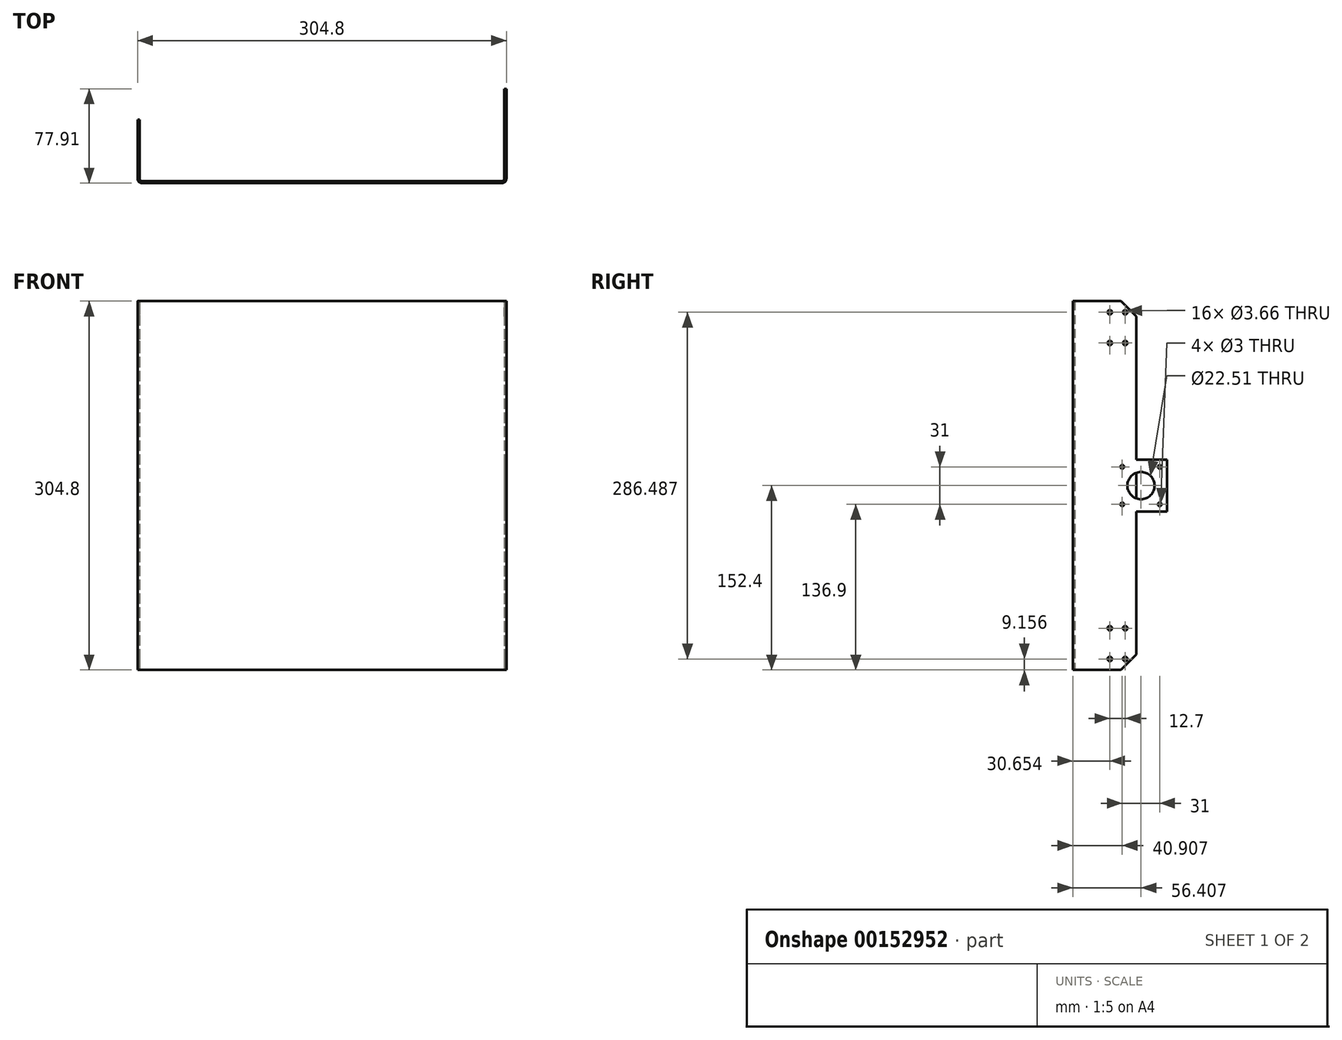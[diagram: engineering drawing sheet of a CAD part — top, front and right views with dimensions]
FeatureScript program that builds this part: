
annotation { "Feature Type Name" : "Feature", "Feature Type Description" : "" }
export const myFeature = defineFeature(function(context is Context, id is Id, definition is map)
    precondition{}
    {
        {
            var Q0;
            Q0=qCreatedBy(makeId("Top.planeOp"),FACE);
            var sketch = newSketch(context, id + "F0", { "sketchPlane" : qUnion([Q0])});
            skLineSegment(sketch, "E0.bottom", {"start": v(0, 0) * mm, "end": v(-301.38, 0) * mm});
            skLineSegment(sketch, "E0.top", {"start": v(1.7, -1.7) * mm, "end": v(-303.1, -1.7) * mm});
            skLineSegment(sketch, "E1.top", {"start": v(-301.38, 50.8) * mm, "end": v(-303.1, 50.8) * mm});
            skLineSegment(sketch, "E1.left", {"start": v(-301.38, 0) * mm, "end": v(-301.38, 50.8) * mm});
            skLineSegment(sketch, "E1.right", {"start": v(-303.1, -1.7) * mm, "end": v(-303.1, 50.8) * mm});
            skLineSegment(sketch, "E2.top", {"start": v(0, 50.8) * mm, "end": v(1.7, 50.8) * mm});
            skLineSegment(sketch, "E2.left", {"start": v(0, 0) * mm, "end": v(0, 50.8) * mm});
            skLineSegment(sketch, "E2.right", {"start": v(1.7, -1.7) * mm, "end": v(1.7, 50.8) * mm});
            skLineSegment(sketch, "E3", {"start": v(-150.7, 0) * mm, "end": v(-150.7, -1.7) * mm, "construction": true});
            skSolve(sketch);
        }
        {
            var Q0;
            Q0=qSketchRegion(id+"F0",true);
            extrude(context, id + "F1", {"entities" : qUnion([Q0]), "depth" : 304.8 * mm});
        }
        {
            var Q0;
            Q0=makeQuery(id+"F1.opExtrude","SWEPT_EDGE",EDGE,{"disambiguationData":[OSD([sQuery(id+"F0.wireOp",EDGE,"E0.top"),sQuery(id+"F0.wireOp",EDGE,"E2.right")])]});
            var Q1;
            Q1=makeQuery(id+"F1.opExtrude","SWEPT_EDGE",EDGE,{"disambiguationData":[OSD([sQuery(id+"F0.wireOp",EDGE,"E0.top"),sQuery(id+"F0.wireOp",EDGE,"E1.right")])]});
            var Q2;
            Q2=makeQuery(id+"FqNnmMD7oaRdpTN_1.opExtrude","CAP_EDGE",EDGE,{"disambiguationData":[OSD([sQuery(id+"FY5sMr6MULj5lJw_1.wireOp",EDGE,"W42EfhJi-fDm4-L9BW-folL-irsYfDskuzBk.top")])],"isStart":false});
            fillet(context, id + "F2", {"entities" : qUnion([Q0, Q1, Q2]), "radius" : 3.7 * mm, "tangentPropagation" : true, "allowEdgeOverflow" : false});
        }
        {
            var Q0;
            Q0=makeQuery(id+"F1.opExtrude","SWEPT_EDGE",EDGE,{"disambiguationData":[OSD([sQuery(id+"F0.wireOp",EDGE,"E0.bottom"),sQuery(id+"F0.wireOp",EDGE,"E2.left")])]});
            var Q1;
            Q1=makeQuery(id+"F1.opExtrude","SWEPT_EDGE",EDGE,{"disambiguationData":[OSD([sQuery(id+"F0.wireOp",EDGE,"E0.bottom"),sQuery(id+"F0.wireOp",EDGE,"E1.left")])]});
            var Q2;
            Q2=makeQuery(id+"FINw0yXB7tfJ6ph_1.opExtrude","CAP_EDGE",EDGE,{"disambiguationData":[OSD([sQuery(id+"FXTh39mUIuS7Wju_1.wireOp",EDGE,"hp9PxWrt-gqSh-sbC0-0nHm-23euh1xvblPI.top")])],"isStart":true});
            fillet(context, id + "F3", {"entities" : qUnion([Q0, Q1, Q2]), "radius" : 1.98 * mm, "tangentPropagation" : true, "allowEdgeOverflow" : false});
        }
        {
            var Q0;
            Q0=makeQuery(id+"F1.opExtrude","SWEPT_FACE",FACE,{"disambiguationData":[OSD([sQuery(id+"F0.wireOp",EDGE,"E2.top")])]});
            var sketch = newSketch(context, id + "F4", { "sketchPlane" : qUnion([Q0])});
            skLineSegment(sketch, "E4.bottom", {"start": v(0, 173.9) * mm, "end": v(-1.7, 173.9) * mm});
            skLineSegment(sketch, "E4.top", {"start": v(0, 130.9) * mm, "end": v(-1.7, 130.9) * mm});
            skLineSegment(sketch, "E4.left", {"start": v(0, 173.9) * mm, "end": v(0, 130.9) * mm});
            skLineSegment(sketch, "E4.right", {"start": v(-1.7, 173.9) * mm, "end": v(-1.7, 130.9) * mm});
            skPoint(sketch, "E5", {"position": v(-1.7, 152.4) * mm});
            skSolve(sketch);
        }
        {
            var Q0;
            Q0 = qSketchRegion(id + "F4", true);
            extrude(context, id + "F5", {"entities" : qUnion([Q0]), "operationType" : NewBodyOperationType.ADD, "depth" : 25.4 * mm});
        }
        {
            var Q0;
            Q0=makeQuery(id+"F5.boolean.opBoolean","MERGE",FACE,{"derivedFrom":[makeQuery(id+"F1.opExtrude","SWEPT_FACE",FACE,{"disambiguationData":[OSD([sQuery(id+"F0.wireOp",EDGE,"E2.right")])]}),makeQuery(id+"F5.opExtrude","SWEPT_FACE",FACE,{"disambiguationData":[OSD([sQuery(id+"F4.wireOp",EDGE,"E4.right")])]})]});
            var sketch = newSketch(context, id + "F6", { "sketchPlane" : qUnion([Q0])});
            skLineSegment(sketch, "E6", {"start": v(76.2, 152.4) * mm, "end": v(54.7, 152.4) * mm, "construction": true});
            skLineSegment(sketch, "E7.bottom", {"start": v(70.2, 136.9) * mm, "end": v(39.2, 136.9) * mm, "construction": true});
            skLineSegment(sketch, "E7.top", {"start": v(70.2, 167.9) * mm, "end": v(39.2, 167.9) * mm, "construction": true});
            skLineSegment(sketch, "E7.left", {"start": v(70.2, 136.9) * mm, "end": v(70.2, 167.9) * mm, "construction": true});
            skLineSegment(sketch, "E7.right", {"start": v(39.2, 136.9) * mm, "end": v(39.2, 167.9) * mm, "construction": true});
            skPoint(sketch, "E7.middle", {"position": v(54.7, 152.4) * mm});
            skCircle(sketch, "E8", {"center": v(54.7, 152.4) * mm, "radius": 11.25 * mm});
            skCircle(sketch, "E9", {"center": v(70.2, 136.9) * mm, "radius": 1.5 * mm});
            skCircle(sketch, "E10", {"center": v(39.2, 136.9) * mm, "radius": 1.5 * mm});
            skCircle(sketch, "E11", {"center": v(39.2, 167.9) * mm, "radius": 1.5 * mm});
            skCircle(sketch, "E12", {"center": v(70.2, 167.9) * mm, "radius": 1.5 * mm});
            skSolve(sketch);
        }
        {
            var Q0;
            Q0 = qSketchRegion(id + "F6", true);
            var Q1;
            Q1=makeQuery(id+"F5.boolean.opBoolean","MERGE",FACE,{"derivedFrom":[makeQuery(id+"F1.opExtrude","SWEPT_FACE",FACE,{"disambiguationData":[OSD([sQuery(id+"F0.wireOp",EDGE,"E2.left")])]}),makeQuery(id+"F5.opExtrude","SWEPT_FACE",FACE,{"disambiguationData":[OSD([sQuery(id+"F4.wireOp",EDGE,"E4.left")])]})]});
            extrude(context, id + "F7", {"entities" : qUnion([Q0]), "operationType" : NewBodyOperationType.REMOVE, "endBound" : BoundingType.UP_TO_SURFACE, "oppositeDirection" : true, "endBoundEntityFace" : qUnion([Q1]), "depth" : 25.4 * mm});
        }
        {
            var Q0;
            Q0=makeQuery(id+"F1.opExtrude","CAP_EDGE",EDGE,{"disambiguationData":[OSD([sQuery(id+"F0.wireOp",EDGE,"E2.top")])],"isStart":true});
            var Q1;
            Q1=makeQuery(id+"F1.opExtrude","CAP_EDGE",EDGE,{"disambiguationData":[OSD([sQuery(id+"F0.wireOp",EDGE,"E1.top")])],"isStart":true});
            var Q2;
            Q2=makeQuery(id+"F1.opExtrude","CAP_EDGE",EDGE,{"disambiguationData":[OSD([sQuery(id+"F0.wireOp",EDGE,"E1.top")])],"isStart":false});
            var Q3;
            Q3=makeQuery(id+"F1.opExtrude","CAP_EDGE",EDGE,{"disambiguationData":[OSD([sQuery(id+"F0.wireOp",EDGE,"E2.top")])],"isStart":false});
            chamfer(context, id + "F8", {"entities" : qUnion([Q0, Q1, Q2, Q3]), "width" : 12.7 * mm, "tangentPropagation" : true});
        }
        {
            var Q0;
            Q0=makeQuery(id+"F5.boolean.opBoolean","MERGE",FACE,{"derivedFrom":[makeQuery(id+"F1.opExtrude","SWEPT_FACE",FACE,{"disambiguationData":[OSD([sQuery(id+"F0.wireOp",EDGE,"E2.right")])]}),makeQuery(id+"F5.opExtrude","SWEPT_FACE",FACE,{"disambiguationData":[OSD([sQuery(id+"F4.wireOp",EDGE,"E4.right")])]})]});
            var sketch = newSketch(context, id + "F9", { "sketchPlane" : qUnion([Q0])});
            skLineSegment(sketch, "E13", {"start": v(44.45, 298.45) * mm, "end": v(41.64, 295.64) * mm, "construction": true});
            skLineSegment(sketch, "E14.bottom", {"start": v(41.64, 295.64) * mm, "end": v(28.94, 295.64) * mm, "construction": true});
            skLineSegment(sketch, "E14.top", {"start": v(41.64, 270.24) * mm, "end": v(28.94, 270.24) * mm, "construction": true});
            skLineSegment(sketch, "E14.left", {"start": v(41.64, 295.64) * mm, "end": v(41.64, 270.24) * mm, "construction": true});
            skLineSegment(sketch, "E14.right", {"start": v(28.94, 295.64) * mm, "end": v(28.94, 270.24) * mm, "construction": true});
            skCircle(sketch, "E15", {"center": v(41.64, 295.64) * mm, "radius": 1.83 * mm});
            skCircle(sketch, "E16", {"center": v(41.64, 270.24) * mm, "radius": 1.83 * mm});
            skCircle(sketch, "E17", {"center": v(28.94, 270.24) * mm, "radius": 1.83 * mm});
            skCircle(sketch, "E18", {"center": v(28.94, 295.64) * mm, "radius": 1.83 * mm});
            skLineSegment(sketch, "E19", {"start": v(44.45, 6.35) * mm, "end": v(41.64, 9.16) * mm, "construction": true});
            skLineSegment(sketch, "E20.bottom", {"start": v(41.64, 9.16) * mm, "end": v(28.94, 9.16) * mm, "construction": true});
            skLineSegment(sketch, "E20.top", {"start": v(41.64, 34.56) * mm, "end": v(28.94, 34.56) * mm, "construction": true});
            skLineSegment(sketch, "E20.left", {"start": v(41.64, 9.16) * mm, "end": v(41.64, 34.56) * mm, "construction": true});
            skLineSegment(sketch, "E20.right", {"start": v(28.94, 9.16) * mm, "end": v(28.94, 34.56) * mm, "construction": true});
            skCircle(sketch, "E21", {"center": v(41.64, 34.56) * mm, "radius": 1.83 * mm});
            skCircle(sketch, "E22", {"center": v(41.64, 9.16) * mm, "radius": 1.83 * mm});
            skCircle(sketch, "E23", {"center": v(28.94, 9.16) * mm, "radius": 1.83 * mm});
            skCircle(sketch, "E24", {"center": v(28.94, 34.56) * mm, "radius": 1.83 * mm});
            skSolve(sketch);
        }
        {
            var Q0;
            Q0 = qSketchRegion(id + "F9", true);
            var Q1;
            Q1=makeQuery(id+"F1.opExtrude","SWEPT_FACE",FACE,{"disambiguationData":[OSD([sQuery(id+"F0.wireOp",EDGE,"E1.right")])]});
            extrude(context, id + "F10", {"entities" : qUnion([Q0]), "operationType" : NewBodyOperationType.REMOVE, "endBound" : BoundingType.UP_TO_SURFACE, "oppositeDirection" : true, "endBoundEntityFace" : qUnion([Q1]), "depth" : 25.4 * mm});
        }
    });
